# Revit family: AFX-Beverly-Outdoor_Sconce-1
name_source: partatom
category: Lighting Fixtures
units: mm (PartAtom-declared; Revit-internal decimal feet)

## family parameters
Cut with Voids When Loaded = No
Host = Face
Light Source = Yes
Part Type = Normal
Room Calculation Point = No
Round Connector Dimension = Use Diameter
Shared = No

## types (2) — shared parameters
Apparent Load = 0 VA
Assembly Code = D5020200
Color Filter = 16777215
Colour Rendering Index = 90
Default Elevation = 48"
Depth = 3 1/2"
Dimming Lamp Color Temperature Shift = <None>
Emit Shape Visible in Rendering = No
Emit from Circle Diameter = 2"
Housing Finish = AFX - Paint Finish Black
Keynote = 12500
Manufacturer = AFX Inc
Power Factor = 1
Product Documentation Link = https://www.afxinc.com
Revit Model Built By = https://www.servex-us.com
Sustainability = https://lamprecycle.org
Tilt Angle = -90.00°
Type Comments = Beverly
URL = https://www.afxinc.com
Voltage = 120 V
Width = 4 1/8"

## per-type parameters (varying)
| type | Description | Distance-L | H-B | H-F | Height | Photometric Web File | Wattage Comments |
| BVYW0406LAJUDBK | LED Outdoor Sconce  - 4 1/8"W x 3 1/2"D x 6 1/4"H | 3 13/16" | 2" | 4 1/4" | 6 1/4" | BVYW0406LAJUDBK_3000K_IES.IES | 10w |
| BVYW0410LAJUDBK | LED Outdoor Sconce  - 4 1/8"W x 3 1/2"D x 10"H | 0" | 5 1/8" | 4 7/8" | 10" | BVYW0410LAJUDSN3000K_IES.IES | 20w |

note: column(s) folded — value = type name in every type: Model

## geometry (parser evidence)
native form markers: Sweep x6
no freeform markers — native parametric forms only
